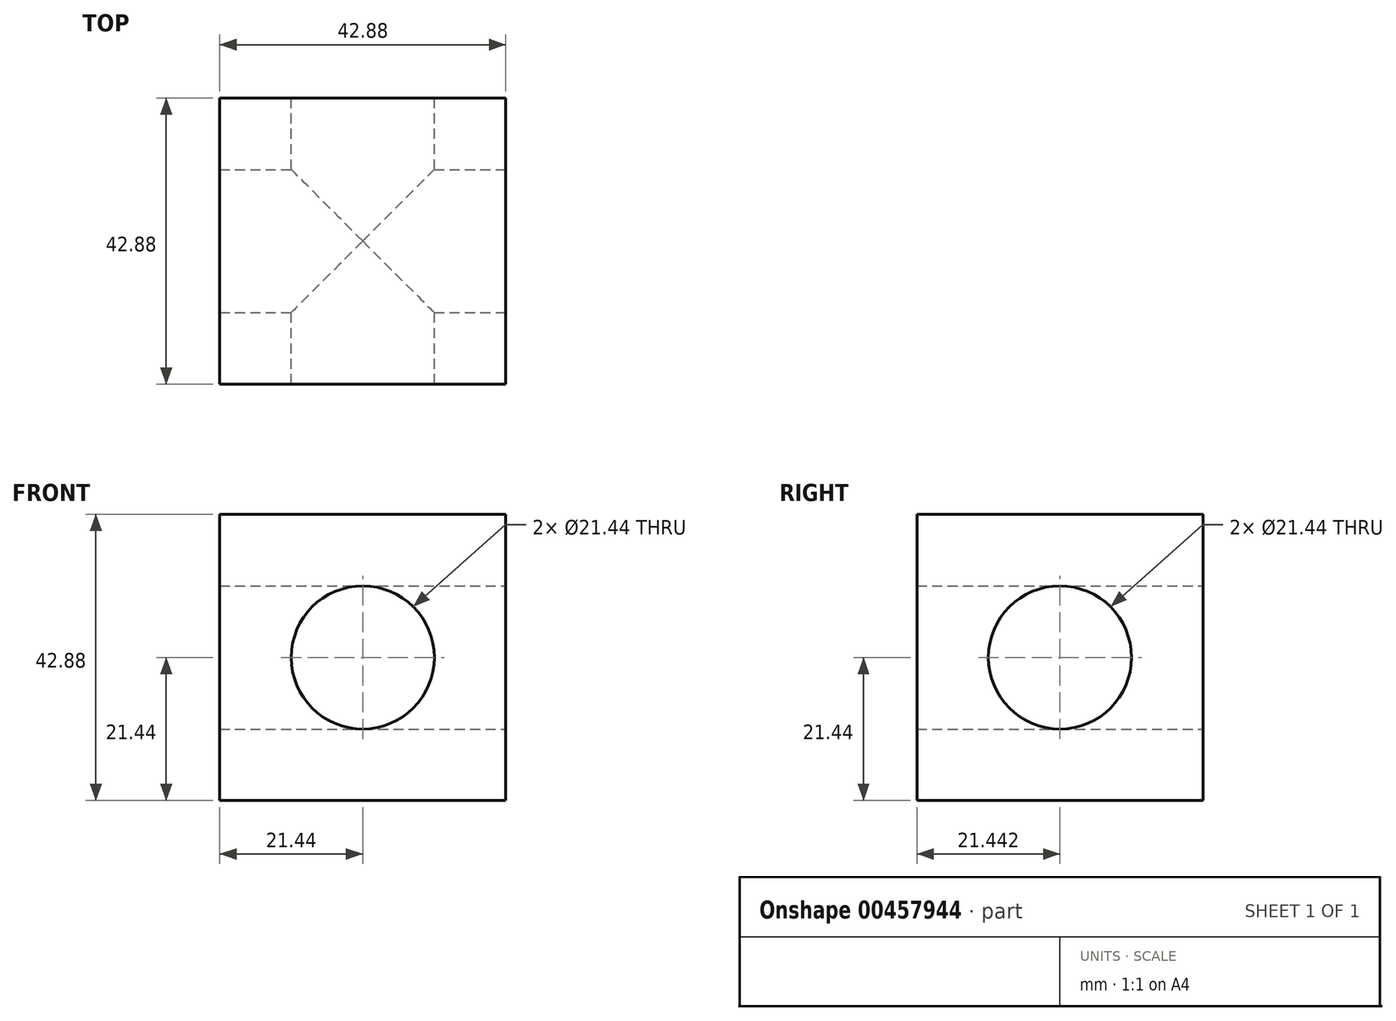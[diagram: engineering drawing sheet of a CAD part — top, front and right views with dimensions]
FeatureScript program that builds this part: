
annotation { "Feature Type Name" : "Feature", "Feature Type Description" : "" }
export const myFeature = defineFeature(function(context is Context, id is Id, definition is map)
    precondition{}
    {
        {
            var Q0;
            Q0=qCreatedBy(makeId("Front.planeOp"),FACE);
            var sketch = newSketch(context, id + "F0", { "sketchPlane" : qUnion([Q0])});
            skLineSegment(sketch, "E0.bottom", {"start": v(-21.44, 21.44) * mm, "end": v(21.44, 21.44) * mm});
            skLineSegment(sketch, "E0.top", {"start": v(-21.44, -21.44) * mm, "end": v(21.44, -21.44) * mm});
            skLineSegment(sketch, "E0.left", {"start": v(-21.44, 21.44) * mm, "end": v(-21.44, -21.44) * mm});
            skLineSegment(sketch, "E0.right", {"start": v(21.44, 21.44) * mm, "end": v(21.44, -21.44) * mm});
            skPoint(sketch, "E0.middle", {"position": v(0, 0) * mm});
            skCircle(sketch, "E1", {"center": v(0, 0) * mm, "radius": 10.72 * mm});
            skSolve(sketch);
        }
        {
            var Q0;
            Q0=makeQuery(id+"F0.imprint","IMPRINT",FACE,{"disambiguationData":[TD([[makeQuery(id+"F0.imprint","IMPRINT",EDGE,{"derivedFrom":sQuery(id+"F0.wireOp",EDGE,"E0.bottom")}),-1.0]])]});
            extrude(context, id + "F1", {"entities" : qUnion([Q0]), "depth" : 42.88 * mm, "offsetDistance" : 25.4 * mm});
        }
        {
            var Q0;
            Q0=makeQuery(id+"F1.opExtrude","SWEPT_FACE",FACE,{"disambiguationData":[OSD([sQuery(id+"F0.wireOp",EDGE,"E0.right")])]});
            var sketch = newSketch(context, id + "F2", { "sketchPlane" : qUnion([Q0])});
            skPoint(sketch, "E2", {"position": v(-42.88, 0) * mm});
            skPoint(sketch, "E3", {"position": v(-21.44, 21.44) * mm});
            skPoint(sketch, "E4", {"position": v(-21.44, 0) * mm});
            skCircle(sketch, "E5", {"center": v(-21.44, 0) * mm, "radius": 10.72 * mm});
            skSolve(sketch);
        }
        {
            var Q0;
            Q0 = qSketchRegion(id + "F2", true);
            var Q1;
            Q1=makeQuery(id+"F1.opExtrude","SWEPT_FACE",FACE,{"disambiguationData":[OSD([sQuery(id+"F0.wireOp",EDGE,"E0.left")])]});
            extrude(context, id + "F3", {"entities" : qUnion([Q0, Q1]), "operationType" : NewBodyOperationType.REMOVE, "oppositeDirection" : true, "depth" : 79.25 * mm, "offsetDistance" : 25.4 * mm});
        }
    });
